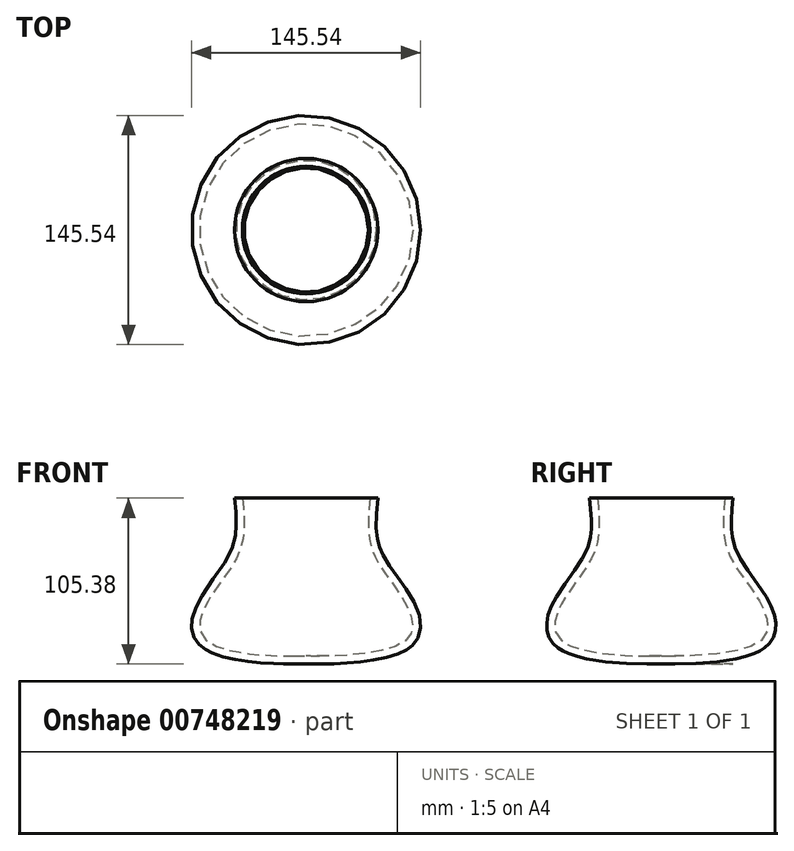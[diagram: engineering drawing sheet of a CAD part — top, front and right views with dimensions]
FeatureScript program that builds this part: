
annotation { "Feature Type Name" : "Feature", "Feature Type Description" : "" }
export const myFeature = defineFeature(function(context is Context, id is Id, definition is map)
    precondition{}
    {
        {
            var Q0;
            Q0=qCreatedBy(makeId("Front.planeOp"),FACE);
            var sketch = newSketch(context, id + "F0", { "sketchPlane" : qUnion([Q0])});
            skFitSpline(sketch, "E0", {"points": [v(41.74, 40.62) * mm, v(41.46, 0) * mm, v(60.3, -30.78) * mm, v(62.26, -60) * mm, v(-3.51, -68.44) * mm, v(-2.95, -68.16) * mm], "startDerivative": vector(-24.42, -181.9) * mm, "endDerivative": vector(34.43, 9.42) * mm});
            skFitSpline(sketch, "E1.0", {"points": [v(46.7, 39.95) * mm, v(46.19, 36.16) * mm, v(45.43, 30.54) * mm, v(44.74, 23.31) * mm, v(44.44, 18.08) * mm, v(44.42, 13.09) * mm, v(44.7, 9.16) * mm, v(45.12, 6.18) * mm, v(45.54, 4.03) * mm, v(45.98, 2.32) * mm, v(46.38, 1) * mm, v(46.83, -0.32) * mm, v(47.47, -1.94) * mm, v(48.66, -4.51) * mm, v(50.42, -7.7) * mm, v(52.93, -11.59) * mm, v(55.75, -15.58) * mm, v(58.79, -19.74) * mm, v(61.93, -24.16) * mm, v(65.08, -28.9) * mm, v(68.1, -34.05) * mm, v(70.68, -39.5) * mm, v(72.17, -44.29) * mm, v(72.71, -48.27) * mm, v(72.71, -51.33) * mm, v(72.2, -54.42) * mm, v(71.08, -57.46) * mm, v(69.6, -59.83) * mm, v(68.12, -61.56) * mm, v(66.87, -62.77) * mm, v(65.7, -63.7) * mm, v(64.71, -64.4) * mm, v(63.68, -65.06) * mm, v(62.35, -65.82) * mm, v(60.09, -66.93) * mm, v(57.06, -68.14) * mm, v(53.13, -69.36) * mm, v(48.96, -70.4) * mm, v(44.57, -71.27) * mm, v(40.04, -72) * mm, v(35.42, -72.6) * mm, v(30.77, -73.07) * mm, v(26.15, -73.44) * mm, v(21.62, -73.71) * mm, v(17.26, -73.9) * mm, v(13.12, -74) * mm, v(9.91, -74.04) * mm, v(7.52, -74.04) * mm, v(5.82, -74.03) * mm, v(4.23, -74) * mm, v(2.75, -73.97) * mm, v(1.38, -73.92) * mm, v(0.14, -73.87) * mm, v(-0.79, -73.81) * mm, v(-1.47, -73.77) * mm, v(-1.95, -73.73) * mm, v(-2.4, -73.7) * mm, v(-2.81, -73.65) * mm, v(-3.2, -73.6) * mm, v(-3.53, -73.56) * mm, v(-3.78, -73.52) * mm, v(-3.98, -73.49) * mm, v(-4.18, -73.45) * mm, v(-4.4, -73.4) * mm, v(-4.66, -73.34) * mm, v(-4.96, -73.25) * mm, v(-5.35, -73.1) * mm, v(-5.81, -72.9) * mm, v(-6.32, -72.59) * mm, v(-6.8, -72.22) * mm, v(-7.38, -71.66) * mm, v(-7.88, -70.95) * mm, v(-8.22, -70.2) * mm, v(-8.42, -69.57) * mm, v(-8.53, -68.89) * mm, v(-8.55, -68.19) * mm, v(-8.47, -67.5) * mm, v(-8.27, -66.68) * mm, v(-7.88, -65.85) * mm, v(-7.38, -65.16) * mm, v(-6.94, -64.7) * mm, v(-6.56, -64.39) * mm, v(-6.15, -64.1) * mm, v(-5.76, -63.88) * mm, v(-5.42, -63.72) * mm, v(-5.16, -63.62) * mm, v(-4.96, -63.55) * mm, v(-4.8, -63.5) * mm, v(-4.6, -63.43) * mm, v(-4.42, -63.38) * mm, v(-4.32, -63.35) * mm, v(-4.27, -63.34) * mm]});
            skLineSegment(sketch, "E2", {"start": v(23.19, 31.34) * mm, "end": v(61.13, 31.34) * mm});
            skLineSegment(sketch, "E3", {"start": v(0, -63.8) * mm, "end": v(0, -80.38) * mm});
            skSolve(sketch);
        }
        {
            var Q0;
            {var subQ0=sQuery(id+"F0.wireOp",EDGE,"E2");var subQ1=sQuery(id+"F0.wireOp",EDGE,"E0");var subQ2=makeQuery(id+"F0.imprint","INTERSECT",VERTEX,{"derivedFrom":[subQ1,subQ0]});Q0=makeQuery(id+"F0.imprint","IMPRINT",FACE,{"disambiguationData":[TD([[makeQuery(id+"F0.imprint","IMPRINT",EDGE,{"disambiguationData":[TD([[subQ2,-1.0]])],"derivedFrom":subQ1}),1.0]])]});}
            var Q1;
            Q1=sQuery(id+"F0.wireOp",EDGE,"E3");
            revolve(context, id + "F1", {"surfaceOperationType" : NewSurfaceOperationType.NEW, "entities" : qUnion([Q0]), "axis" : qUnion([Q1]), "revolveType" : RevolveType.FULL});
        }
    });
